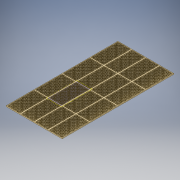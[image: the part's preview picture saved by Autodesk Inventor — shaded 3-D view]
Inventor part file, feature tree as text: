
AUTODESK INVENTOR PART (.ipt)
format: ipt  version: 2018 (Build 220112000, 112)  size: 8,456,192 bytes
history: native  units: in
note: dims shown in document units (in); Inventor stores cm internally (conversion verified against a paired STEP export)
features: pattern_linear x3, extrude x2, sketch x2, plane x1
ambient origin geometry x8: Origin, YZ Plane, XZ Plane, XY Plane, X Axis, Y Axis, Z Axis, Center Point
bodies: Solid1 (feature_tree)
feature tree (8):
  extrude  "Extrusion1"  Depth=240.0in
  extrude  "Extrusion2"  Depth=10.0in
  plane  "Work Plane1"
  pattern_linear  "Rectangular Pattern1"  Spacing1=10.0in  [1 undecoded]
  pattern_linear  "Rectangular Pattern2"  Count1=21 Spacing1=11.0in
  pattern_linear  "Rectangular Pattern3"  Spacing1=1.0in  [1 undecoded]
  sketch  "Sketch1"  dims[d0=120.0in d1=240.0in]
  sketch  "Sketch2"  dims[d2=7.0in d3=0.0in d4=10.0in d5=10.0in d6=8.2677in d8=11.0in d9=3.937in d11=11.0in d14=1.0in d15=0.0in d16=90.0deg d17=0.7874in d19=120.0in d20=0.7874in d22=240.0in d23=0.7874in d25=240.0in d26=0.7874in d28=480.0in]
note: 2 required parameter values undecoded (feature->parameter linkage not recoverable at this tier; creation-order binding heuristic only, values carry confidence <= 0.55)
